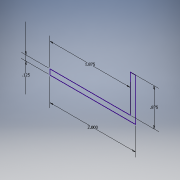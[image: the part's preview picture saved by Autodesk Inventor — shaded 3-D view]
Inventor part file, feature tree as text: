
AUTODESK INVENTOR PART (.ipt)
format: ipt  version: 2016 (Build 200138000, 138)  size: 113,664 bytes
history: native  units: in
note: dims shown in document units (in); Inventor stores cm internally (conversion verified against a paired STEP export)
features: other x3, sketch x3
ambient origin geometry x8: Origin, YZ Plane, XZ Plane, XY Plane, X Axis, Y Axis, Z Axis, Center Point
bodies: Solid1 (feature_tree)
feature tree (6):
  other  "rail gusset .ipt"
  other  "Solid1::rail gusset .ipt"
  other  "TaggingFeature1"
  sketch  "Sketch1"  dims[d0=0.3937in]
  sketch  "Sketch2"
  sketch  "Sketch3"
